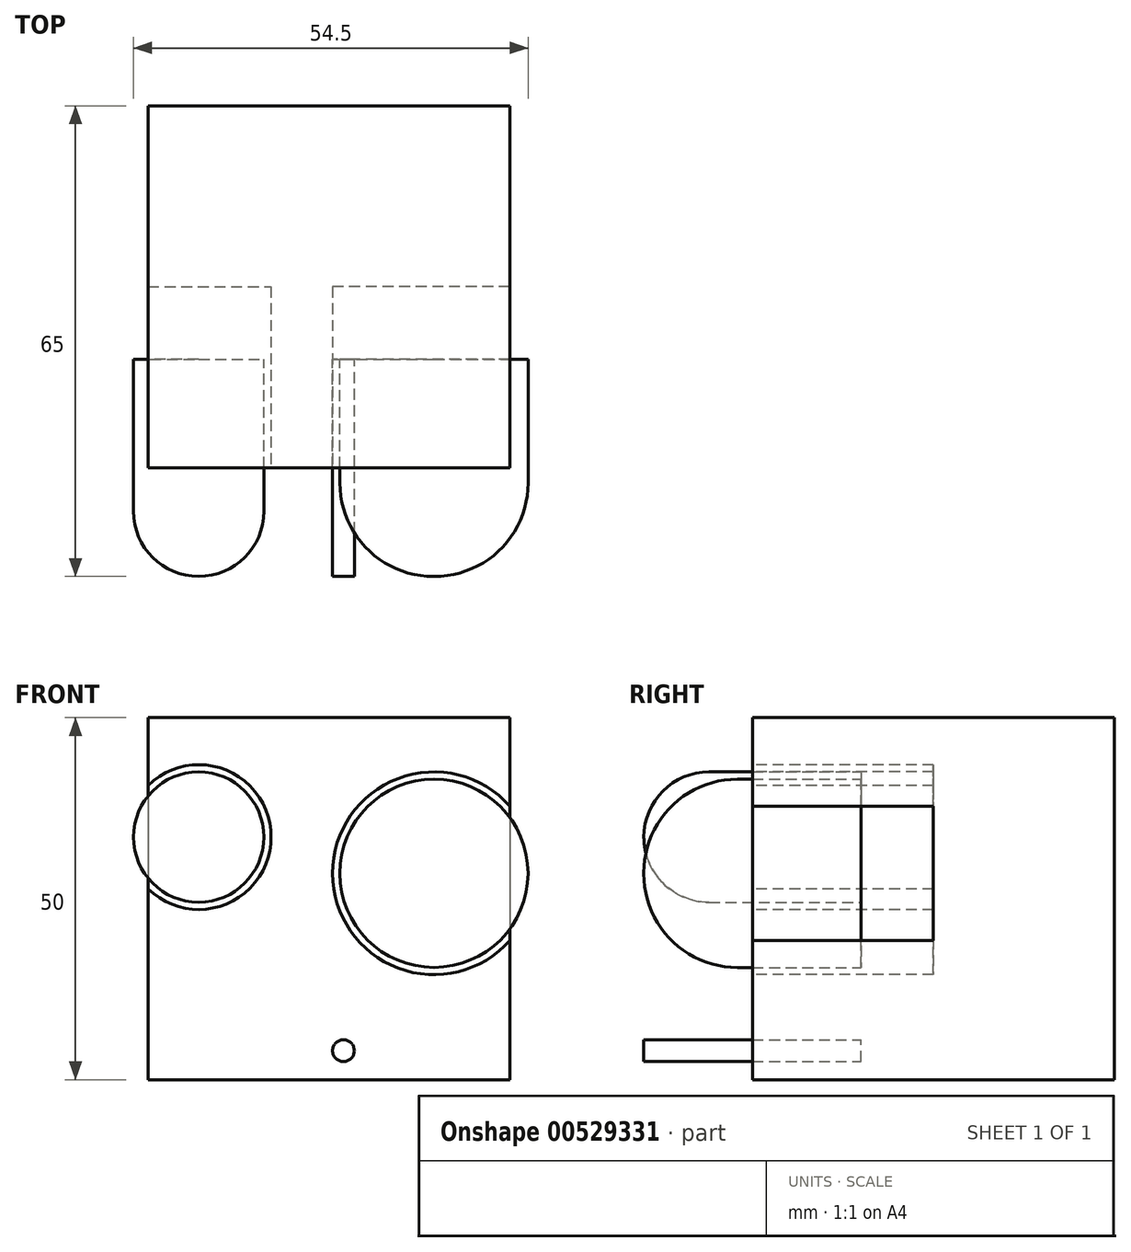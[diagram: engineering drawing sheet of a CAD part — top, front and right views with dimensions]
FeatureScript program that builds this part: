
annotation { "Feature Type Name" : "Feature", "Feature Type Description" : "" }
export const myFeature = defineFeature(function(context is Context, id is Id, definition is map)
    precondition{}
    {
        {
            var Q0;
            Q0=qCreatedBy(makeId("Front.planeOp"),FACE);
            var sketch = newSketch(context, id + "F0", { "sketchPlane" : qUnion([Q0])});
            skLineSegment(sketch, "E0.bottom", {"start": v(-25, 25) * mm, "end": v(25, 25) * mm});
            skLineSegment(sketch, "E0.top", {"start": v(-25, -25) * mm, "end": v(25, -25) * mm});
            skLineSegment(sketch, "E0.left", {"start": v(-25, 25) * mm, "end": v(-25, -25) * mm});
            skLineSegment(sketch, "E0.right", {"start": v(25, 25) * mm, "end": v(25, -25) * mm});
            skSolve(sketch);
        }
        {
            var Q0;
            Q0 = qSketchRegion(id + "F0", true);
            extrude(context, id + "F1", {"entities" : qUnion([Q0]), "depth" : 50 * mm, "offsetDistance" : 25 * mm});
        }
        {
            var Q0;
            Q0=makeQuery(id+"F1.opExtrude","CAP_FACE",FACE,{"disambiguationData":[OSD([sQuery(id+"F0.wireOp",EDGE,"E0.bottom"),sQuery(id+"F0.wireOp",EDGE,"E0.top"),sQuery(id+"F0.wireOp",EDGE,"E0.left"),sQuery(id+"F0.wireOp",EDGE,"E0.right")])],"isStart":false});
            var sketch = newSketch(context, id + "F2", { "sketchPlane" : qUnion([Q0])});
            skCircle(sketch, "E1", {"center": v(-18, 8.5) * mm, "radius": 9 * mm});
            skCircle(sketch, "E2", {"center": v(14.5, 3.5) * mm, "radius": 13 * mm});
            skCircle(sketch, "E3", {"center": v(2, -21) * mm, "radius": 1.5 * mm});
            skSolve(sketch);
        }
        {
            var Q0;
            Q0 = qSketchRegion(id + "F2", true);
            extrude(context, id + "F3", {"entities" : qUnion([Q0]), "endBound" : BoundingType.SYMMETRIC, "depth" : 30 * mm, "offsetDistance" : 25 * mm});
        }
        {
            var Q0;
            Q0=makeQuery(id+"F1.opExtrude","CAP_FACE",FACE,{"disambiguationData":[OSD([sQuery(id+"F0.wireOp",EDGE,"E0.bottom"),sQuery(id+"F0.wireOp",EDGE,"E0.top"),sQuery(id+"F0.wireOp",EDGE,"E0.left"),sQuery(id+"F0.wireOp",EDGE,"E0.right")])],"isStart":false});
            var sketch = newSketch(context, id + "F4", { "sketchPlane" : qUnion([Q0])});
            skArc(sketch, "E4", {"start": v(-25, 1.36) * mm, "mid": v(-8, 8.5) * mm, "end": v(-25, 15.64) * mm});
            skArc(sketch, "E5", {"start": v(25, 12.76) * mm, "mid": v(0.5, 3.5) * mm, "end": v(25, -5.76) * mm});
            skLineSegment(sketch, "E6", {"start": v(-25, 15.64) * mm, "end": v(-25, 1.36) * mm});
            skLineSegment(sketch, "E7", {"start": v(25, 12.76) * mm, "end": v(25, -5.76) * mm});
            skSolve(sketch);
        }
        {
            var Q0;
            Q0 = qSketchRegion(id + "F4", true);
            extrude(context, id + "F5", {"entities" : qUnion([Q0]), "oppositeDirection" : true, "depth" : 25 * mm, "offsetDistance" : 25 * mm});
        }
        {
            var Q0;
            Q0=makeQuery(id+"F3.opExtrude","CAP_EDGE",EDGE,{"disambiguationData":[OSD([sQuery(id+"F2.wireOp",EDGE,"E2")])],"isStart":false});
            fillet(context, id + "F6", {"entities" : qUnion([Q0]), "radius" : 12.9 * mm, "tangentPropagation" : true, "allowEdgeOverflow" : false});
        }
        {
            var Q0;
            Q0=makeQuery(id+"F3.opExtrude","CAP_EDGE",EDGE,{"disambiguationData":[OSD([sQuery(id+"F2.wireOp",EDGE,"E1")])],"isStart":false});
            fillet(context, id + "F7", {"entities" : qUnion([Q0]), "radius" : 9 * mm, "tangentPropagation" : true, "allowEdgeOverflow" : false});
        }
    });
